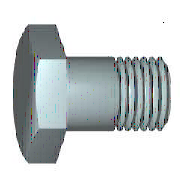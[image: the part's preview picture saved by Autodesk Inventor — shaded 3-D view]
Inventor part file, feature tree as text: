
AUTODESK INVENTOR PART (.ipt)
format: ipt  version: 2021 (Build 250183000, 183)  size: 192,000 bytes
history: native  units: mm (DEFAULTED — no unit token found)
features: sketch x3, extrude x1, chamfer x1, plane x1
ambient origin geometry x7: Origin, YZ Plane, XZ Plane, X Axis, Y Axis, Z Axis, Center Point
bodies: Solid1 (feature_tree), Body (feature_tree)
feature tree (6):
  extrude  "Head"  Depth=18.0mm
  chamfer  "Chamfer1"  Distance=3.5mm
  plane  "Work Plane1"
  sketch  "Sketch1"  dims[d0=30.0mm d1=18.0mm]
  sketch  "Sketch2"  dims[d2=6.0mm]
  sketch  "Sketch4"  dims[d12=90.0deg d3=3.5mm d4=0.0mm d5=30.0deg d21=90.0deg d6=0.61345mm d7=0.61355mm d8=0.0mm d9=0.5001mm d10=8.88mm d11=10.0mm d13=0.61355mm d14=6.0mm d15=18.0mm d16=0.0mm d19=10.0mm d55=45.0deg d57=0.0mm d58=0.0mm]
